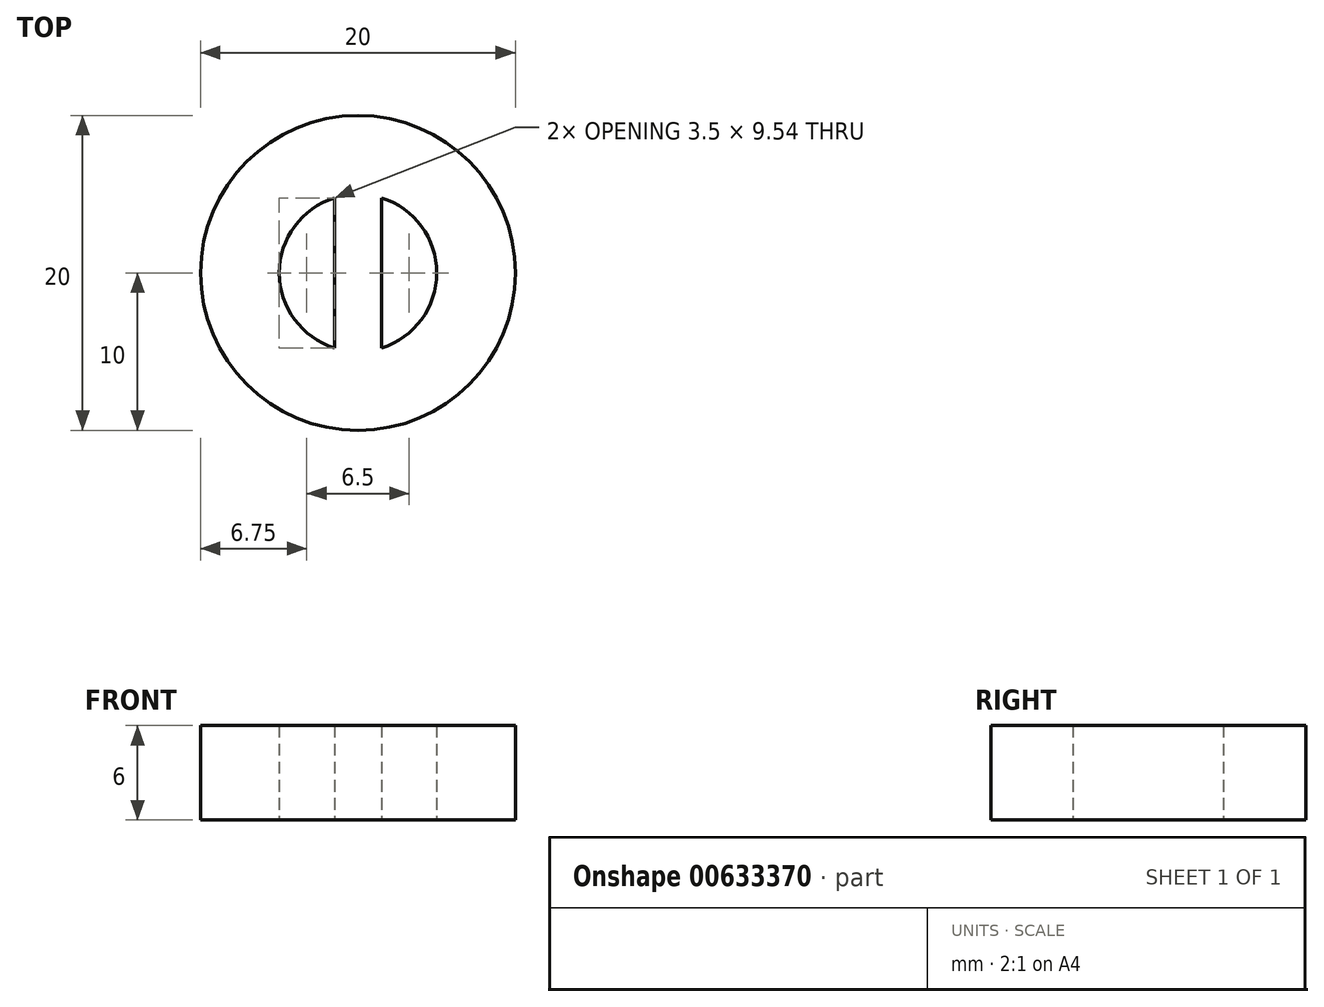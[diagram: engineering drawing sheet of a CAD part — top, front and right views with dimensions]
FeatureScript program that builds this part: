
annotation { "Feature Type Name" : "Feature", "Feature Type Description" : "" }
export const myFeature = defineFeature(function(context is Context, id is Id, definition is map)
    precondition{}
    {
        {
            var Q0;
            Q0=qCreatedBy(makeId("Top.planeOp"),FACE);
            var sketch = newSketch(context, id + "F0", { "sketchPlane" : qUnion([Q0])});
            skCircle(sketch, "E0", {"center": v(0, 0) * mm, "radius": 5 * mm});
            skCircle(sketch, "E1", {"center": v(0, 0) * mm, "radius": 10 * mm});
            skLineSegment(sketch, "E2.bottom", {"start": v(1.5, -5.72) * mm, "end": v(-1.5, -5.72) * mm});
            skLineSegment(sketch, "E2.top", {"start": v(1.5, 5.72) * mm, "end": v(-1.5, 5.72) * mm});
            skLineSegment(sketch, "E2.left", {"start": v(1.5, -5.72) * mm, "end": v(1.5, 5.72) * mm});
            skLineSegment(sketch, "E2.right", {"start": v(-1.5, -5.72) * mm, "end": v(-1.5, 5.72) * mm});
            skSolve(sketch);
        }
        {
            var Q0;
            Q0=makeQuery(id+"F0.imprint","IMPRINT",FACE,{"disambiguationData":[TD([[makeQuery(id+"F0.imprint","IMPRINT",EDGE,{"derivedFrom":sQuery(id+"F0.wireOp",EDGE,"E1")}),1.0]])]});
            var Q1;
            {var subQ0=sQuery(id+"F0.wireOp",EDGE,"E2.right");var subQ1=sQuery(id+"F0.wireOp",EDGE,"E0");var subQ2=makeQuery(id+"F0.imprint","INTERSECT",VERTEX,{"disambiguationData":[OD(0.0)],"derivedFrom":[subQ1,subQ0]});Q1=makeQuery(id+"F0.imprint","IMPRINT",FACE,{"disambiguationData":[TD([[makeQuery(id+"F0.imprint","IMPRINT",EDGE,{"disambiguationData":[TD([[subQ2,-1.0]])],"derivedFrom":subQ1}),1.0]])]});}
            var Q2;
            {var subQ0=sQuery(id+"F0.wireOp",EDGE,"E2.left");var subQ1=sQuery(id+"F0.wireOp",EDGE,"E0");var subQ2=makeQuery(id+"F0.imprint","INTERSECT",VERTEX,{"disambiguationData":[OD(0.0)],"derivedFrom":[subQ1,subQ0]});Q2=makeQuery(id+"F0.imprint","IMPRINT",FACE,{"disambiguationData":[TD([[makeQuery(id+"F0.imprint","IMPRINT",EDGE,{"disambiguationData":[TD([[subQ2,1.0]])],"derivedFrom":subQ1}),1.0]])]});}
            var Q3;
            {var subQ5=sQuery(id+"F0.wireOp",EDGE,"E2.top");Q3=makeQuery(id+"F0.imprint","IMPRINT",FACE,{"disambiguationData":[TD([[makeQuery(id+"F0.imprint","IMPRINT",EDGE,{"derivedFrom":subQ5}),1.0]])]});}
            var Q4;
            {var subQ5=sQuery(id+"F0.wireOp",EDGE,"E2.bottom");Q4=makeQuery(id+"F0.imprint","IMPRINT",FACE,{"disambiguationData":[TD([[makeQuery(id+"F0.imprint","IMPRINT",EDGE,{"derivedFrom":subQ5}),-1.0]])]});}
            extrude(context, id + "F1", {"entities" : qUnion([Q0, Q1, Q2, Q3, Q4]), "depth" : 6 * mm, "hasOffset" : true, "offsetDistance" : 6 * mm});
        }
    });
